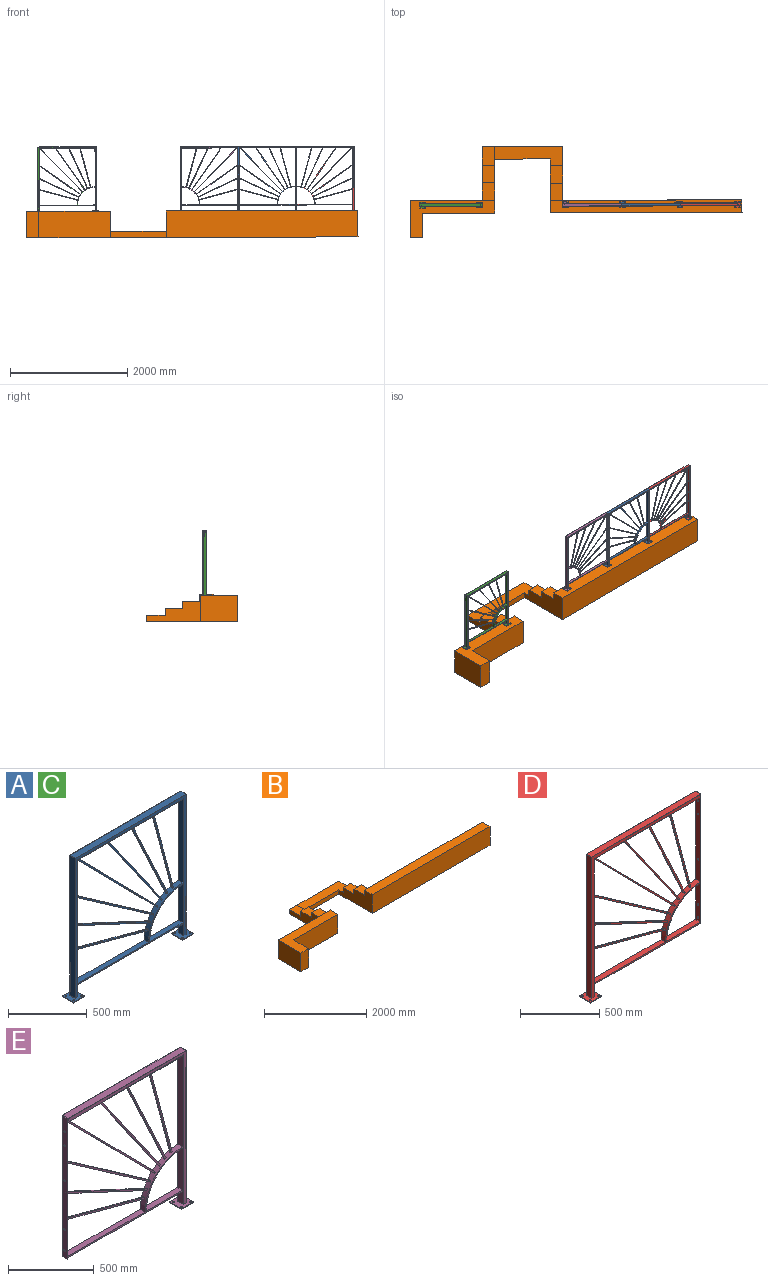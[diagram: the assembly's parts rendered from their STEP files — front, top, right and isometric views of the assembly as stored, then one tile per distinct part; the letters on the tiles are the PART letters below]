
ASSEMBLY  parts=5 mates=4
PART A: 73 faces, bbox 1075x100x1095 mm
  f0: plane 100x5mm, normal (0,1,0), area 500mm2, adj f1,f7,f8,f9
  f1: plane 100x5mm, normal (-1,0,0), area 500mm2, adj f0,f2,f8,f9
  f2: plane 100x5mm, normal (0,-1,0), area 500mm2, adj f1,f7,f8,f9
  f3: cylinder r=6mm len=12mm, axis (0,0,1), area 188.5mm2, adj f8,f9
  f4: cylinder r=6mm len=12mm, axis (0,0,1), area 188.5mm2, adj f8,f9
  f5: cylinder r=6mm len=12mm, axis (0,0,1), area 188.5mm2, adj f8,f9
  f6: cylinder r=6mm len=12mm, axis (0,0,1), area 188.5mm2, adj f8,f9
  f7: plane 100x5mm, normal (1,0,0), area 500mm2, adj f0,f2,f8,f9
  f8: plane 100x100mm, normal (0,0,-1), area 9547.6mm2, adj f0,f1,f2,f3,f4,f5,f6,f7
  f9: plane 100x100mm, normal (0,0,1), area 8297.6mm2, adj f0,f1,f2,f3,f4,f5,f6,f7
  f10: plane 100x5mm, normal (0,1,0), area 500mm2, adj f11,f17,f18,f19
  f11: plane 100x5mm, normal (-1,0,0), area 500mm2, adj f10,f12,f18,f19
  f12: plane 100x5mm, normal (0,-1,0), area 500mm2, adj f11,f17,f18,f19
  f13: cylinder r=6mm len=12mm, axis (0,0,1), area 188.5mm2, adj f18,f19
  f14: cylinder r=6mm len=12mm, axis (0,0,1), area 188.5mm2, adj f18,f19
  f15: cylinder r=6mm len=12mm, axis (0,0,1), area 188.5mm2, adj f18,f19
  f16: cylinder r=6mm len=12mm, axis (0,0,1), area 188.5mm2, adj f18,f19
  f17: plane 100x5mm, normal (1,0,0), area 500mm2, adj f10,f12,f18,f19
  f18: plane 100x100mm, normal (0,0,-1), area 9547.6mm2, adj f10,f11,f12,f13,f14,f15,f16,f17
  f19: plane 100x100mm, normal (0,0,1), area 8297.6mm2, adj f10,f11,f12,f13,f14,f15,f16,f17
  f20: cylinder r=300mm len=300mm, axis (0,1,0), area 18849.6mm2, adj f22,f23,f52,f53
  f21: cylinder r=310mm len=310mm, axis (0,1,0), area 18777.8mm2, adj f22,f23,f24,f25,f26,f27,f28,f29
  f22: plane 950x320mm, normal (0,-1,0), area 14290.9mm2, adj f20,f21,f52,f53,f54,f61,f62
  f23: plane 950x320mm, normal (0,1,0), area 14290.9mm2, adj f20,f21,f52,f53,f54,f61,f62
  f24: plane 673.42x314.02mm, normal (0.42,0,0.91), area 7430.3mm2, adj f21,f26,f27,f54
  f25: plane 669.04x311.98mm, normal (-0.42,0,-0.91), area 7382.1mm2, adj f21,f26,f27,f54
  f26: plane 673.42x323.01mm, normal (0,-1,0), area 7405.9mm2, adj f21,f24,f25,f54
  f27: plane 673.42x323.01mm, normal (0,1,0), area 7405.9mm2, adj f21,f24,f25,f54
  f28: plane 701.93x491.5mm, normal (0.57,0,0.82), area 8569mm2, adj f21,f30,f31,f54
  f29: plane 696.06x487.39mm, normal (-0.57,0,-0.82), area 8497.4mm2, adj f21,f30,f31,f54
  f30: plane 701.93x499.6mm, normal (0,-1,0), area 8532.9mm2, adj f21,f28,f29,f54
  f31: plane 701.93x499.6mm, normal (0,1,0), area 8532.9mm2, adj f21,f28,f29,f54
  f32: plane 665.56x178.34mm, normal (-0.97,0,-0.26), area 6890.4mm2, adj f21,f34,f35,f55
  f33: plane 663.13x177.69mm, normal (0.97,0,0.26), area 6865.2mm2, adj f21,f34,f35,f55
  f34: plane 665.56x188.04mm, normal (0,-1,0), area 6877.6mm2, adj f21,f32,f33,f55
  f35: plane 665.56x188.04mm, normal (0,1,0), area 6877.6mm2, adj f21,f32,f33,f55
  f36: plane 679.96x317.07mm, normal (0.91,0,0.42), area 7502.6mm2, adj f21,f38,f39,f55
  f37: plane 684.04x318.98mm, normal (-0.91,0,-0.42), area 7547.6mm2, adj f21,f38,f39,f55
  f38: plane 684.04x328.11mm, normal (0,-1,0), area 7524.8mm2, adj f21,f36,f37,f55
  f39: plane 684.04x328.11mm, normal (0,1,0), area 7524.8mm2, adj f21,f36,f37,f55
  f40: plane 653.31x175.05mm, normal (0.26,0,0.97), area 6763.5mm2, adj f21,f42,f43,f54
  f41: plane 650.56x174.32mm, normal (-0.26,0,-0.97), area 6735.1mm2, adj f21,f42,f43,f54
  f42: plane 653.31x184.67mm, normal (0,-1,0), area 6749.1mm2, adj f21,f40,f41,f54
  f43: plane 653.31x184.67mm, normal (0,1,0), area 6749.1mm2, adj f21,f40,f41,f54
  f44: plane 737.19x725.73mm, normal (0.71,0,0.7), area 10344.7mm2, adj f21,f46,f47,f55
  f45: plane 744.09x732.52mm, normal (-0.71,0,-0.7), area 10441.5mm2, adj f21,f46,f47,f54
  f46: plane 744.09x739.76mm, normal (0,-1,0), area 10392.8mm2, adj f21,f44,f45,f55
  f47: plane 744.09x739.76mm, normal (0,1,0), area 10392.8mm2, adj f21,f44,f45,f55
  f48: plane 705.46x493.97mm, normal (0.82,0,0.57), area 8612.1mm2, adj f21,f50,f51,f55
  f49: plane 711.06x497.89mm, normal (-0.82,0,-0.57), area 8680.5mm2, adj f21,f50,f51,f55
  f50: plane 711.06x506.18mm, normal (0,-1,0), area 8646mm2, adj f21,f48,f49,f55
  f51: plane 711.06x506.18mm, normal (0,1,0), area 8646mm2, adj f21,f48,f49,f55
  f52: plane 1065x50mm, normal (-1,0,0), area 52450mm2, adj f19,f20,f21,f22,f23,f53,f55,f59
  f53: plane 300x40mm, normal (0,0,1), area 12000mm2, adj f20,f22,f23,f52
  f54: plane 1065x50mm, normal (1,0,0), area 52514.1mm2, adj f9,f22,f23,f24,f25,f26,f27,f28
  f55: plane 950x50mm, normal (0,0,-1), area 47023.7mm2, adj f32,f33,f34,f35,f36,f37,f38,f39
  f56: plane 1090x50mm, normal (1,0,0), area 54500mm2, adj f19,f57,f59,f60
  f57: plane 1000x50mm, normal (0,0,1), area 50000mm2, adj f56,f58,f59,f60
  f58: plane 1090x50mm, normal (-1,0,0), area 54500mm2, adj f9,f57,f59,f60
  f59: plane 1090x1000mm, normal (0,-1,0), area 78250mm2, adj f9,f19,f52,f54,f55,f56,f57,f58
  f60: plane 1090x1000mm, normal (0,1,0), area 78250mm2, adj f9,f19,f52,f54,f55,f56,f57,f58
  f61: plane 640x40mm, normal (0,0,1), area 25600mm2, adj f21,f22,f23,f54
  f62: plane 950x40mm, normal (0,0,-1), area 38000mm2, adj f22,f23,f52,f54
  f63: plane 994x44mm, normal (0,0,-1), area 43736mm2, adj f64,f68,f69,f70
  f64: plane 1087x44mm, normal (-1,0,0), area 47828mm2, adj f63,f65,f68,f69
  f65: plane 44x19mm, normal (0,0,1), area 836mm2, adj f64,f66,f68,f69
  f66: plane 1068x44mm, normal (1,0,0), area 46992mm2, adj f65,f67,f68,f69
  f67: plane 956x44mm, normal (0,0,1), area 42064mm2, adj f66,f68,f69,f71
  f68: plane 1087x994mm, normal (0,1,0), area 59470mm2, adj f63,f64,f65,f66,f67,f70,f71,f72
  f69: plane 1087x994mm, normal (0,-1,0), area 59470mm2, adj f63,f64,f65,f66,f67,f70,f71,f72
  f70: plane 1087x44mm, normal (1,0,0), area 47828mm2, adj f63,f68,f69,f72
  f71: plane 1068x44mm, normal (-1,0,0), area 46992mm2, adj f67,f68,f69,f72
  f72: plane 44x19mm, normal (0,0,1), area 836mm2, adj f68,f69,f70,f71
PART B: 27 faces, bbox 5651.1x1550x450 mm
  f0: plane 3260x450mm, normal (0,1,0), area 1397700mm2, adj f1,f3,f4,f5,f7,f8
  f1: plane 920x450mm, normal (-1,0,0), area 268450mm2, adj f0,f2,f4,f5,f6,f8,f9,f10
  f2: plane 3260x450mm, normal (0,-1,0), area 1467000mm2, adj f1,f3,f4,f5
  f3: plane 450x215mm, normal (1,0,0), area 96750mm2, adj f0,f2,f4,f5
  f4: plane 3260x215mm, normal (0,0,1), area 700900mm2, adj f0,f1,f2,f3
  f5: plane 5651.07x1550mm, normal (0,0,-1), area 1690605.8mm2, adj f0,f1,f2,f3,f7,f11,f13,f14
  f6: plane 210x115mm, normal (0,1,0), area 24150mm2, adj f1,f7,f8,f10
  f7: plane 920x330mm, normal (1,0,0), area 193200mm2, adj f0,f5,f6,f8,f9,f10,f11,f12
  f8: plane 290x210mm, normal (0,0,1), area 60900mm2, adj f0,f1,f6,f7
  f9: plane 210x115mm, normal (0,1,0), area 24150mm2, adj f1,f7,f10,f12
  f10: plane 300x210mm, normal (0,0,1), area 63000mm2, adj f1,f6,f7,f9
  f11: plane 1371.07x105mm, normal (0,1,0), area 138157.4mm2, adj f5,f7,f12,f14,f22,f26
  f12: plane 1161.07x330mm, normal (0,0,1), area 273780.8mm2, adj f1,f7,f9,f11,f13,f14
  f13: plane 951.07x100mm, normal (0,-1,0), area 95107.4mm2, adj f1,f5,f12,f14
  f14: plane 1135x450mm, normal (1,0,0), area 277400mm2, adj f5,f11,f12,f13,f15,f19,f20,f21
  f15: plane 1440x450mm, normal (0,1,0), area 577650mm2, adj f5,f14,f16,f20,f22,f23
  f16: plane 630x450mm, normal (-1,0,0), area 283500mm2, adj f5,f15,f17,f20
  f17: plane 450x215mm, normal (0,-1,0), area 96750mm2, adj f5,f16,f18,f20
  f18: plane 450x415mm, normal (1,0,0), area 186750mm2, adj f5,f17,f19,f20
  f19: plane 1225x450mm, normal (0,-1,0), area 551250mm2, adj f5,f14,f18,f20
  f20: plane 1440x630mm, normal (0,0,1), area 398825mm2, adj f14,f15,f16,f17,f18,f19
  f21: plane 210x110mm, normal (0,1,0), area 23100mm2, adj f14,f22,f23,f25
  f22: plane 920x335mm, normal (-1,0,0), area 202150mm2, adj f5,f11,f15,f21,f23,f24,f25,f26
  f23: plane 305x210mm, normal (0,0,1), area 64050mm2, adj f14,f15,f21,f22
  f24: plane 210x120mm, normal (0,1,0), area 25200mm2, adj f14,f22,f25,f26
  f25: plane 295x210mm, normal (0,0,1), area 61950mm2, adj f14,f21,f22,f24
  f26: plane 320x210mm, normal (0,0,1), area 67200mm2, adj f11,f14,f22,f24
PART C: same geometry as A
PART D: 71 faces, bbox 1017.5x100x1095 mm
  f0: plane 50x25mm, normal (1,0,0), area 214mm2, adj f1,f2,f3,f16,f17,f48,f55,f56
  f1: plane 975x50mm, normal (0,0,1), area 48750mm2, adj f0,f2,f3,f49
  f2: plane 1090x975mm, normal (0,-1,0), area 51000mm2, adj f0,f1,f13,f47,f48,f49
  f3: plane 1090x975mm, normal (0,1,0), area 51000mm2, adj f0,f1,f13,f47,f48,f49
  f4: plane 100x5mm, normal (0,1,0), area 500mm2, adj f5,f11,f12,f13
  f5: plane 100x5mm, normal (-1,0,0), area 500mm2, adj f4,f6,f12,f13
  f6: plane 100x5mm, normal (0,-1,0), area 500mm2, adj f5,f11,f12,f13
  f7: cylinder r=6mm len=12mm, axis (0,0,1), area 188.5mm2, adj f12,f13
  f8: cylinder r=6mm len=12mm, axis (0,0,1), area 188.5mm2, adj f12,f13
  f9: cylinder r=6mm len=12mm, axis (0,0,1), area 188.5mm2, adj f12,f13
  f10: cylinder r=6mm len=12mm, axis (0,0,1), area 188.5mm2, adj f12,f13
  f11: plane 100x5mm, normal (1,0,0), area 500mm2, adj f4,f6,f12,f13
  f12: plane 100x100mm, normal (0,0,-1), area 9547.6mm2, adj f4,f5,f6,f7,f8,f9,f10,f11
  f13: plane 100x100mm, normal (0,0,1), area 8297.6mm2, adj f2,f3,f4,f5,f6,f7,f8,f9
  f14: cylinder r=300mm len=300mm, axis (0,1,0), area 18849.6mm2, adj f16,f17,f46,f62
  f15: cylinder r=310mm len=310mm, axis (0,1,0), area 18777.8mm2, adj f16,f17,f18,f19,f20,f21,f22,f23
  f16: plane 1004x955mm, normal (0,-1,0), area 19310.9mm2, adj f0,f14,f15,f46,f47,f50,f51,f59
  f17: plane 1004x955mm, normal (0,1,0), area 19310.9mm2, adj f0,f14,f15,f46,f47,f50,f51,f59
  f18: plane 673.42x314.02mm, normal (0.42,0,0.91), area 7430.3mm2, adj f15,f20,f21,f47
  f19: plane 669.04x311.98mm, normal (-0.42,0,-0.91), area 7382.1mm2, adj f15,f20,f21,f47
  f20: plane 673.42x323.01mm, normal (0,-1,0), area 7405.9mm2, adj f15,f18,f19,f47
  f21: plane 673.42x323.01mm, normal (0,1,0), area 7405.9mm2, adj f15,f18,f19,f47
  f22: plane 701.93x491.5mm, normal (0.57,0,0.82), area 8569mm2, adj f15,f24,f25,f47
  f23: plane 696.06x487.39mm, normal (-0.57,0,-0.82), area 8497.4mm2, adj f15,f24,f25,f47
  f24: plane 701.93x499.6mm, normal (0,-1,0), area 8532.9mm2, adj f15,f22,f23,f47
  f25: plane 701.93x499.6mm, normal (0,1,0), area 8532.9mm2, adj f15,f22,f23,f47
  f26: plane 665.56x178.34mm, normal (-0.97,0,-0.26), area 6890.4mm2, adj f15,f28,f29,f48
  f27: plane 663.13x177.69mm, normal (0.97,0,0.26), area 6865.2mm2, adj f15,f28,f29,f48
  f28: plane 665.56x188.04mm, normal (0,-1,0), area 6877.6mm2, adj f15,f26,f27,f48
  f29: plane 665.56x188.04mm, normal (0,1,0), area 6877.6mm2, adj f15,f26,f27,f48
  f30: plane 679.96x317.07mm, normal (0.91,0,0.42), area 7502.6mm2, adj f15,f32,f33,f48
  f31: plane 684.04x318.98mm, normal (-0.91,0,-0.42), area 7547.6mm2, adj f15,f32,f33,f48
  f32: plane 684.04x328.11mm, normal (0,-1,0), area 7524.8mm2, adj f15,f30,f31,f48
  f33: plane 684.04x328.11mm, normal (0,1,0), area 7524.8mm2, adj f15,f30,f31,f48
  f34: plane 653.31x175.05mm, normal (0.26,0,0.97), area 6763.5mm2, adj f15,f36,f37,f47
  f35: plane 650.56x174.32mm, normal (-0.26,0,-0.97), area 6735.1mm2, adj f15,f36,f37,f47
  f36: plane 653.31x184.67mm, normal (0,-1,0), area 6749.1mm2, adj f15,f34,f35,f47
  f37: plane 653.31x184.67mm, normal (0,1,0), area 6749.1mm2, adj f15,f34,f35,f47
  f38: plane 737.19x725.73mm, normal (0.71,0,0.7), area 10344.7mm2, adj f15,f40,f41,f48
  f39: plane 744.09x732.52mm, normal (-0.71,0,-0.7), area 10441.5mm2, adj f15,f40,f41,f47
  f40: plane 744.09x739.76mm, normal (0,-1,0), area 10392.8mm2, adj f15,f38,f39,f48
  f41: plane 744.09x739.76mm, normal (0,1,0), area 10392.8mm2, adj f15,f38,f39,f48
  f42: plane 705.46x493.97mm, normal (0.82,0,0.57), area 8612.1mm2, adj f15,f44,f45,f48
  f43: plane 711.06x497.89mm, normal (-0.82,0,-0.57), area 8680.5mm2, adj f15,f44,f45,f48
  f44: plane 711.06x506.18mm, normal (0,-1,0), area 8646mm2, adj f15,f42,f43,f48
  f45: plane 711.06x506.18mm, normal (0,1,0), area 8646mm2, adj f15,f42,f43,f48
  f46: plane 300x40mm, normal (0,0,1), area 12000mm2, adj f14,f16,f17,f62
  f47: plane 1065x50mm, normal (1,0,0), area 52514.1mm2, adj f2,f3,f13,f16,f17,f18,f19,f20
  f48: plane 950x50mm, normal (0,0,-1), area 47023.7mm2, adj f0,f2,f3,f26,f27,f28,f29,f30
  f49: plane 1090x50mm, normal (-1,0,0), area 54500mm2, adj f1,f2,f3,f13
  f50: plane 640x40mm, normal (0,0,1), area 25600mm2, adj f15,f16,f17,f47
  f51: plane 950x40mm, normal (0,0,-1), area 38000mm2, adj f16,f17,f47,f61
  f52: plane 1068x44mm, normal (-1,0,0), area 46992mm2, adj f53,f55,f56,f58
  f53: plane 44x19mm, normal (0,0,1), area 836mm2, adj f52,f54,f55,f56
  f54: plane 1087x44mm, normal (1,0,0), area 47828mm2, adj f53,f55,f56,f57
  f55: plane 1087x972mm, normal (0,-1,0), area 38760mm2, adj f0,f52,f53,f54,f57,f58
  f56: plane 1087x972mm, normal (0,1,0), area 38760mm2, adj f0,f52,f53,f54,f57,f58
  f57: plane 972x44mm, normal (0,0,-1), area 42768mm2, adj f0,f54,f55,f56,f59
  f58: plane 953x44mm, normal (0,0,1), area 41932mm2, adj f0,f52,f55,f56,f59
  f59: plane 40x19mm, normal (-1,0,0), area 760mm2, adj f16,f17,f57,f58
  f60: plane 655x40mm, normal (-1,0,0), area 25860.7mm2, adj f15,f16,f17,f48,f68,f69,f70
  f61: plane 40x5mm, normal (-1,0,0), area 200mm2, adj f16,f17,f51,f64
  f62: plane 300x40mm, normal (-1,0,0), area 11773.8mm2, adj f14,f16,f17,f46,f66,f67
  f63: plane 40x5mm, normal (0,0,1), area 200mm2, adj f0,f16,f17,f65
  f64: plane 40x5mm, normal (0,0,-1), area 200mm2, adj f16,f17,f61,f65
  f65: plane 1004x40mm, normal (1,0,0), area 39594.5mm2, adj f16,f17,f63,f64,f66,f67,f68,f69
  f66: cylinder r=6mm len=12mm, axis (1,0,0), area 188.5mm2, adj f62,f65
  f67: cylinder r=6mm len=12mm, axis (1,0,0), area 188.5mm2, adj f62,f65
  f68: cylinder r=6mm len=12mm, axis (1,0,0), area 188.5mm2, adj f60,f65
  f69: cylinder r=6mm len=12mm, axis (1,0,0), area 188.5mm2, adj f60,f65
  f70: cylinder r=6mm len=12mm, axis (1,0,0), area 188.5mm2, adj f60,f65
PART E: 70 faces, bbox 1017.5x100x1095 mm
  f0: plane 50x25mm, normal (-1,0,0), area 214mm2, adj f3,f4,f35,f37,f38,f39,f55,f56
  f1: cylinder r=300mm len=300mm, axis (0,1,0), area 18849.6mm2, adj f3,f4,f33,f34
  f2: cylinder r=310mm len=310mm, axis (0,1,0), area 18777.8mm2, adj f3,f4,f5,f6,f7,f8,f9,f10
  f3: plane 1004x955mm, normal (0,-1,0), area 19310.9mm2, adj f0,f1,f2,f33,f34,f40,f41,f59
  f4: plane 1004x955mm, normal (0,1,0), area 19310.9mm2, adj f0,f1,f2,f33,f34,f40,f41,f59
  f5: plane 673.42x314.02mm, normal (0.42,0,0.91), area 7430.3mm2, adj f2,f7,f8,f61
  f6: plane 669.04x311.98mm, normal (-0.42,0,-0.91), area 7382.1mm2, adj f2,f7,f8,f61
  f7: plane 673.42x323.01mm, normal (0,-1,0), area 7405.9mm2, adj f2,f5,f6,f61
  f8: plane 673.42x323.01mm, normal (0,1,0), area 7405.9mm2, adj f2,f5,f6,f61
  f9: plane 701.93x491.5mm, normal (0.57,0,0.82), area 8569mm2, adj f2,f11,f12,f61
  f10: plane 696.06x487.39mm, normal (-0.57,0,-0.82), area 8497.4mm2, adj f2,f11,f12,f61
  f11: plane 701.93x499.6mm, normal (0,-1,0), area 8532.9mm2, adj f2,f9,f10,f61
  f12: plane 701.93x499.6mm, normal (0,1,0), area 8532.9mm2, adj f2,f9,f10,f61
  f13: plane 665.56x178.34mm, normal (-0.97,0,-0.26), area 6890.4mm2, adj f2,f15,f16,f35
  f14: plane 663.13x177.69mm, normal (0.97,0,0.26), area 6865.2mm2, adj f2,f15,f16,f35
  f15: plane 665.56x188.04mm, normal (0,-1,0), area 6877.6mm2, adj f2,f13,f14,f35
  f16: plane 665.56x188.04mm, normal (0,1,0), area 6877.6mm2, adj f2,f13,f14,f35
  f17: plane 679.96x317.07mm, normal (0.91,0,0.42), area 7502.6mm2, adj f2,f19,f20,f35
  f18: plane 684.04x318.98mm, normal (-0.91,0,-0.42), area 7547.6mm2, adj f2,f19,f20,f35
  f19: plane 684.04x328.11mm, normal (0,-1,0), area 7524.8mm2, adj f2,f17,f18,f35
  f20: plane 684.04x328.11mm, normal (0,1,0), area 7524.8mm2, adj f2,f17,f18,f35
  f21: plane 653.31x175.05mm, normal (0.26,0,0.97), area 6763.5mm2, adj f2,f23,f24,f61
  f22: plane 650.56x174.32mm, normal (-0.26,0,-0.97), area 6735.1mm2, adj f2,f23,f24,f61
  f23: plane 653.31x184.67mm, normal (0,-1,0), area 6749.1mm2, adj f2,f21,f22,f61
  f24: plane 653.31x184.67mm, normal (0,1,0), area 6749.1mm2, adj f2,f21,f22,f61
  f25: plane 737.19x725.73mm, normal (0.71,0,0.7), area 10344.7mm2, adj f2,f27,f28,f35
  f26: plane 744.09x732.52mm, normal (-0.71,0,-0.7), area 10441.5mm2, adj f2,f27,f28,f61
  f27: plane 744.09x739.76mm, normal (0,-1,0), area 10392.8mm2, adj f2,f25,f26,f35
  f28: plane 744.09x739.76mm, normal (0,1,0), area 10392.8mm2, adj f2,f25,f26,f35
  f29: plane 705.46x493.97mm, normal (0.82,0,0.57), area 8612.1mm2, adj f2,f31,f32,f35
  f30: plane 711.06x497.89mm, normal (-0.82,0,-0.57), area 8680.5mm2, adj f2,f31,f32,f35
  f31: plane 711.06x506.18mm, normal (0,-1,0), area 8646mm2, adj f2,f29,f30,f35
  f32: plane 711.06x506.18mm, normal (0,1,0), area 8646mm2, adj f2,f29,f30,f35
  f33: plane 1065x50mm, normal (-1,0,0), area 52450mm2, adj f1,f2,f3,f4,f34,f35,f38,f39
  f34: plane 300x40mm, normal (0,0,1), area 12000mm2, adj f1,f3,f4,f33
  f35: plane 950x50mm, normal (0,0,-1), area 47023.7mm2, adj f0,f13,f14,f15,f16,f17,f18,f19
  f36: plane 1090x50mm, normal (1,0,0), area 54500mm2, adj f37,f38,f39,f42
  f37: plane 975x50mm, normal (0,0,1), area 48750mm2, adj f0,f36,f38,f39
  f38: plane 1090x975mm, normal (0,-1,0), area 51000mm2, adj f0,f33,f35,f36,f37,f42
  f39: plane 1090x975mm, normal (0,1,0), area 51000mm2, adj f0,f33,f35,f36,f37,f42
  f40: plane 640x40mm, normal (0,0,1), area 25600mm2, adj f2,f3,f4,f61
  f41: plane 950x40mm, normal (0,0,-1), area 38000mm2, adj f3,f4,f33,f59
  f42: plane 100x100mm, normal (0,0,1), area 8297.6mm2, adj f33,f36,f38,f39,f43,f44,f45,f46
  f43: plane 100x5mm, normal (0,1,0), area 500mm2, adj f42,f44,f50,f51
  f44: plane 100x5mm, normal (-1,0,0), area 500mm2, adj f42,f43,f45,f51
  f45: plane 100x5mm, normal (0,-1,0), area 500mm2, adj f42,f44,f50,f51
  f46: cylinder r=6mm len=12mm, axis (0,0,1), area 188.5mm2, adj f42,f51
  f47: cylinder r=6mm len=12mm, axis (0,0,1), area 188.5mm2, adj f42,f51
  f48: cylinder r=6mm len=12mm, axis (0,0,1), area 188.5mm2, adj f42,f51
  f49: cylinder r=6mm len=12mm, axis (0,0,1), area 188.5mm2, adj f42,f51
  f50: plane 100x5mm, normal (1,0,0), area 500mm2, adj f42,f43,f45,f51
  f51: plane 100x100mm, normal (0,0,-1), area 9547.6mm2, adj f43,f44,f45,f46,f47,f48,f49,f50
  f52: plane 1087x44mm, normal (-1,0,0), area 47828mm2, adj f53,f55,f56,f57
  f53: plane 44x19mm, normal (0,0,1), area 836mm2, adj f52,f54,f55,f56
  f54: plane 1068x44mm, normal (1,0,0), area 46992mm2, adj f53,f55,f56,f58
  f55: plane 1087x972mm, normal (0,-1,0), area 38760mm2, adj f0,f52,f53,f54,f57,f58
  f56: plane 1087x972mm, normal (0,1,0), area 38760mm2, adj f0,f52,f53,f54,f57,f58
  f57: plane 972x44mm, normal (0,0,-1), area 42768mm2, adj f0,f52,f55,f56,f60
  f58: plane 953x44mm, normal (0,0,1), area 41932mm2, adj f0,f54,f55,f56,f60
  f59: plane 40x5mm, normal (1,0,0), area 200mm2, adj f3,f4,f41,f64
  f60: plane 40x19mm, normal (1,0,0), area 760mm2, adj f3,f4,f57,f58
  f61: plane 965x40mm, normal (1,0,0), area 37698.6mm2, adj f3,f4,f5,f6,f7,f8,f9,f10
  f62: plane 40x5mm, normal (0,0,1), area 200mm2, adj f0,f3,f4,f63
  f63: plane 1004x40mm, normal (-1,0,0), area 39594.5mm2, adj f3,f4,f62,f64,f65,f66,f67,f68
  f64: plane 40x5mm, normal (0,0,-1), area 200mm2, adj f3,f4,f59,f63
  f65: cylinder r=6mm len=12mm, axis (-1,0,0), area 188.5mm2, adj f61,f63
  f66: cylinder r=6mm len=12mm, axis (-1,0,0), area 188.5mm2, adj f61,f63
  f67: cylinder r=6mm len=12mm, axis (-1,0,0), area 188.5mm2, adj f61,f63
  f68: cylinder r=6mm len=12mm, axis (-1,0,0), area 188.5mm2, adj f61,f63
  f69: cylinder r=6mm len=12mm, axis (-1,0,0), area 188.5mm2, adj f61,f63
PLACE A rot(axis=(0.57,-0.58,0.58),0.3deg) t=(3593.1,-82.73,1924.09)mm
PLACE B rot(axis=(0.57,-0.58,0.58),0.3deg) t=(-11.39,-13.58,369.32)mm
PLACE C rot(axis=(0.57,-0.58,0.58),0.3deg) t=(187.05,-92.19,1914.67)mm
PLACE D rot(axis=(0,0,-1),179.8deg) t=(5573.09,-77.22,1929.56)mm
PLACE E rot(axis=(0,0,-1),179.8deg) t=(3613.1,-82.67,1924.14)mm
MATE fastened E.f51 <-> B.f4  axis (0,0,-1) through (2578.49,-32.6,826.42)mm
MATE fastened C.f18 <-> B.f20  axis (0,0,-1) through (1227.43,-36.35,822.68)mm
MATE fastened E.f63 <-> A.f58  axis (1,0,0) through (3593.1,-82.72,1923.09)mm
MATE fastened D.f65 <-> A.f56  axis (-1,0,0) through (4593.1,-79.94,1925.85)mm
